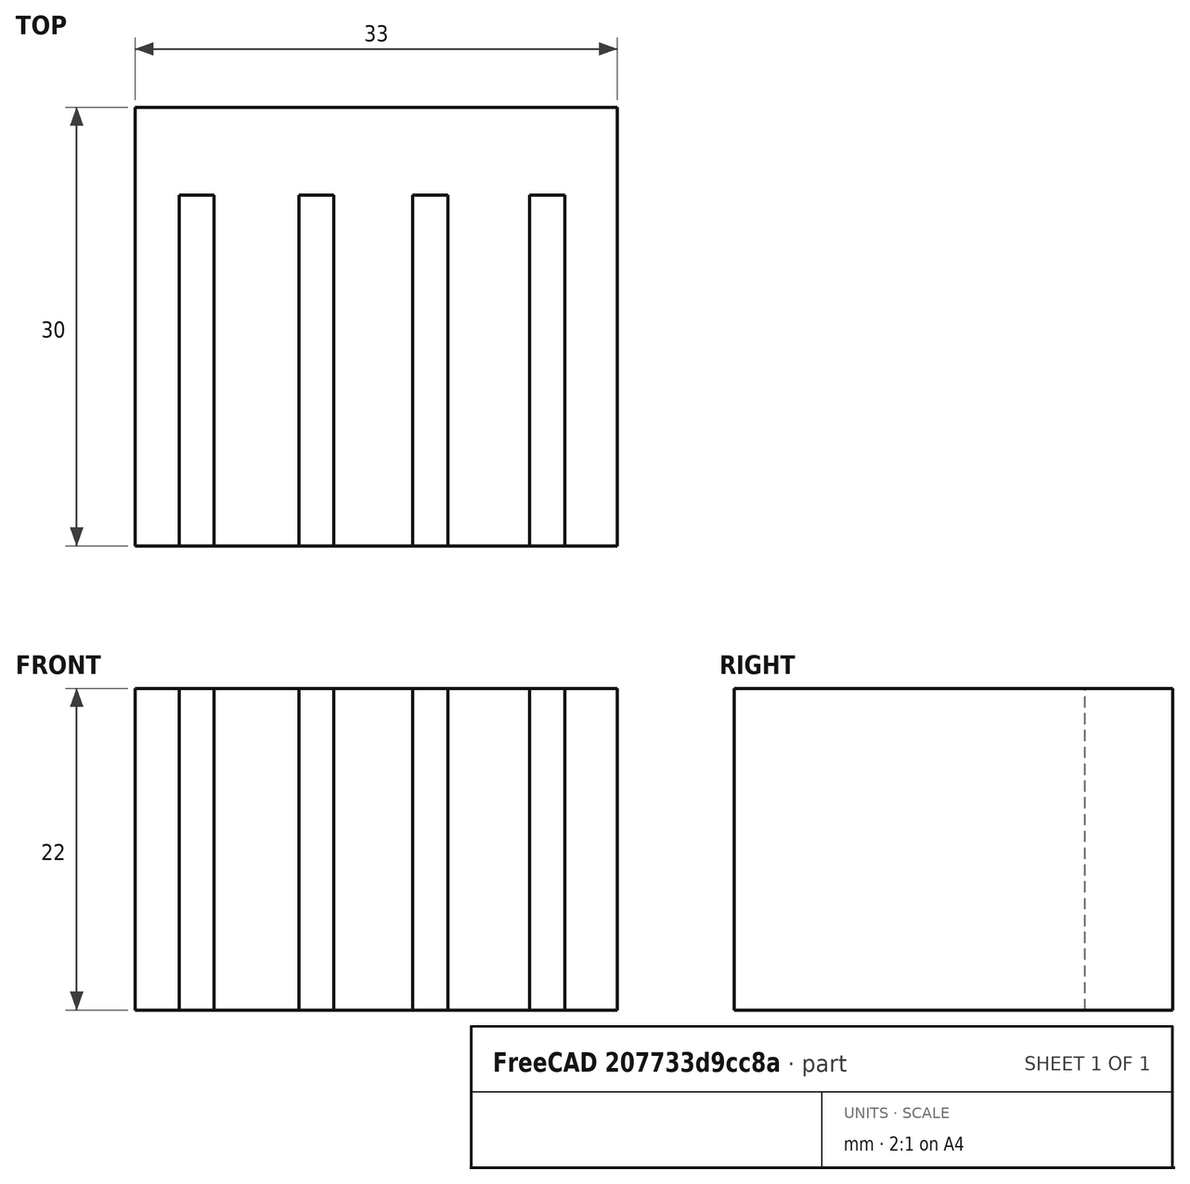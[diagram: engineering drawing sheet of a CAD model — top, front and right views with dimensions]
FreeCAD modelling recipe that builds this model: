
FCSTD DOCUMENT  (FreeCAD 1.0R39319 (Git))
Label: ojt1_t08r01_sdholder
License: All rights reserved
LicenseURL: https://en.wikipedia.org/wiki/All_rights_reserved
objects: Part::Box×5, Part::MultiFuse×1
note: 6 computed .brp shape members not serialized (recipe doc carries the construction recipe); baked Part::Feature solids carry a one-line shape summary decoded from their .brp

FEATURE [Part::Box] Box  label="Cube"
  AttacherType = Attacher::AttachEngine3D
  Height = 23
  Length = 2.4
  Placement = pos=(3,0,0) rot=(0,0,1;0rad)
  Width = 24
FEATURE [Part::Box] Box001  label="Cube001"
  AttacherType = Attacher::AttachEngine3D
  Height = 23
  Length = 2.4
  Placement = pos=(11.2,0,0) rot=(0,0,1;0rad)
  Width = 24
FEATURE [Part::Box] Box002  label="Cube002"
  AttacherType = Attacher::AttachEngine3D
  Height = 23
  Length = 2.4
  Placement = pos=(19,0,0) rot=(0,0,1;0rad)
  Width = 24
FEATURE [Part::Box] Box003  label="Cube003"
  AttacherType = Attacher::AttachEngine3D
  Height = 23
  Length = 2.4
  Placement = pos=(27,0,0) rot=(0,0,1;0rad)
  Width = 24
FEATURE [Part::MultiFuse] Fusion
  Refine = true
  Shapes = -> [Box,Box001,Box002,Box003]
FEATURE [Part::Box] Box004  label="Cube004"
  AttacherType = Attacher::AttachEngine3D
  Height = 22
  Length = 33
  Width = 30
